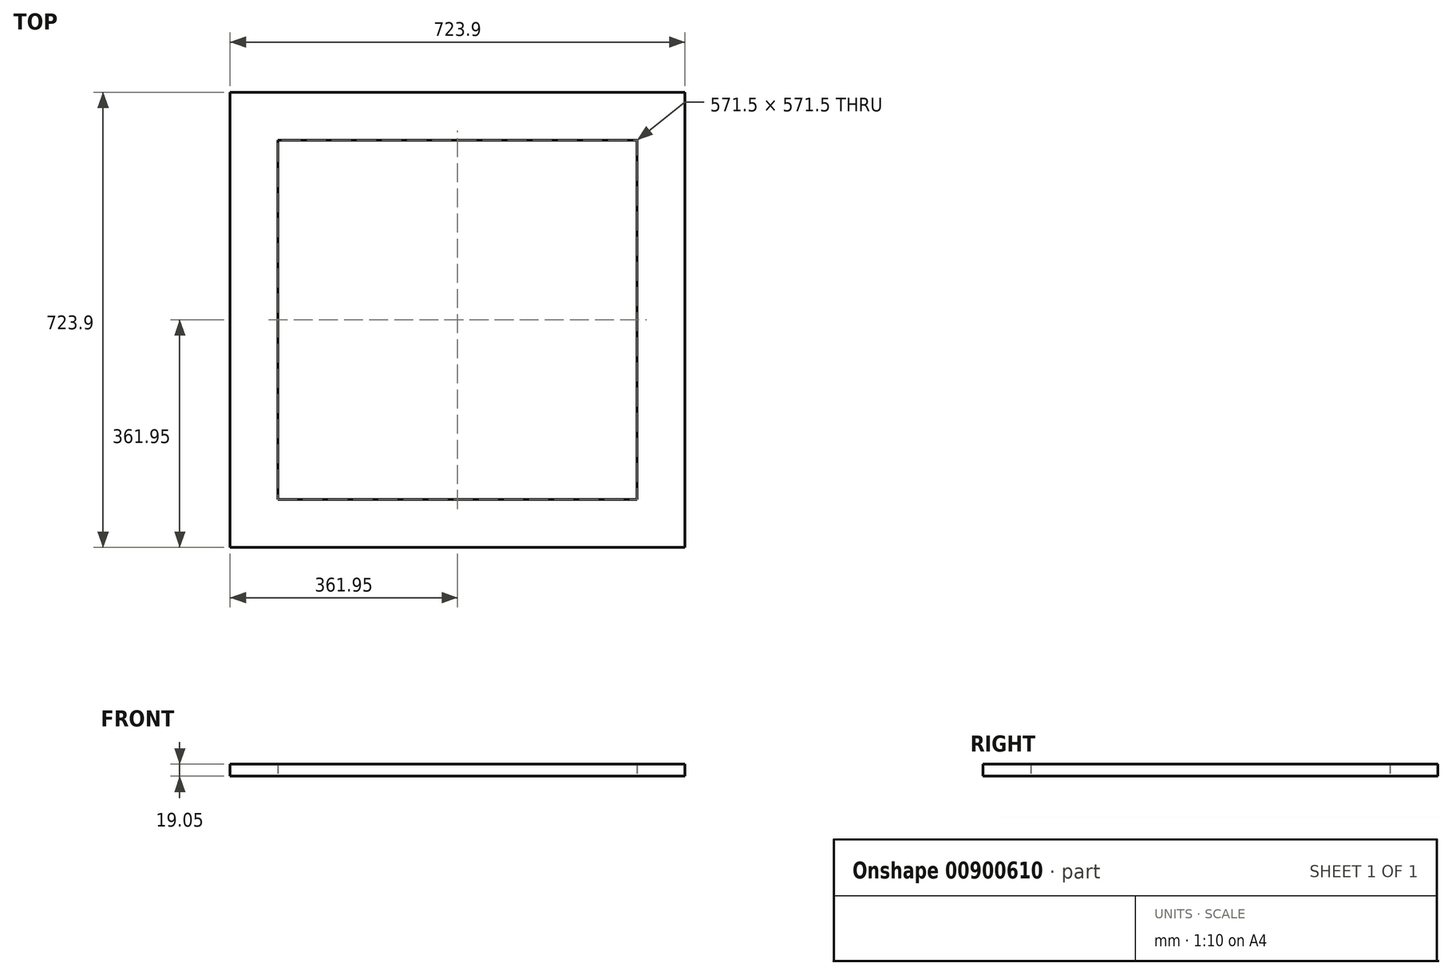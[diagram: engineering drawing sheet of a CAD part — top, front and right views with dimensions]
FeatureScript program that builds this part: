
annotation { "Feature Type Name" : "Feature", "Feature Type Description" : "" }
export const myFeature = defineFeature(function(context is Context, id is Id, definition is map)
    precondition{}
    {
        {
            var Q0;
            Q0=qCreatedBy(makeId("Top.planeOp"),FACE);
            var sketch = newSketch(context, id + "F0", { "sketchPlane" : qUnion([Q0])});
            skLineSegment(sketch, "E0.bottom", {"start": v(361.95, 361.95) * mm, "end": v(-361.95, 361.95) * mm});
            skLineSegment(sketch, "E0.top", {"start": v(361.95, -361.95) * mm, "end": v(-361.95, -361.95) * mm});
            skLineSegment(sketch, "E0.left", {"start": v(361.95, 361.95) * mm, "end": v(361.95, -361.95) * mm});
            skLineSegment(sketch, "E0.right", {"start": v(-361.95, 361.95) * mm, "end": v(-361.95, -361.95) * mm});
            skPoint(sketch, "E0.middle", {"position": v(0, 0) * mm});
            skLineSegment(sketch, "E1.bottom", {"start": v(-285.75, 285.75) * mm, "end": v(285.75, 285.75) * mm});
            skLineSegment(sketch, "E1.top", {"start": v(-285.75, -285.75) * mm, "end": v(285.75, -285.75) * mm});
            skLineSegment(sketch, "E1.left", {"start": v(-285.75, 285.75) * mm, "end": v(-285.75, -285.75) * mm});
            skLineSegment(sketch, "E1.right", {"start": v(285.75, 285.75) * mm, "end": v(285.75, -285.75) * mm});
            skSolve(sketch);
        }
        {
            var Q0;
            Q0=makeQuery(id+"F0.imprint","IMPRINT",FACE,{"disambiguationData":[TD([[makeQuery(id+"F0.imprint","IMPRINT",EDGE,{"derivedFrom":sQuery(id+"F0.wireOp",EDGE,"E0.bottom")}),1.0]])]});
            extrude(context, id + "F1", {"entities" : qUnion([Q0]), "depth" : 19.05 * mm, "offsetDistance" : 25.4 * mm});
        }
    });
